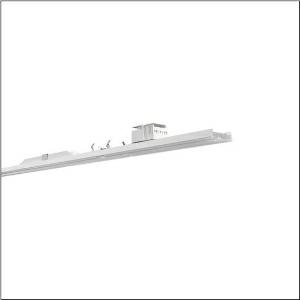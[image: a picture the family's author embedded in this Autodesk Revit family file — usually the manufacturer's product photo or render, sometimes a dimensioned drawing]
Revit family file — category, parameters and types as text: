
# Revit family: licross_r__11_recessed_mo_51tl19cn48xf_739b
name_source: partatom
category: Lighting Fixtures
units: mm (PartAtom-declared; Revit-internal decimal feet)

## family parameters
Cut with Voids When Loaded = No
Host = Face
Light Source = No
Part Type = Normal
Room Calculation Point = No
Round Connector Dimension = Use Diameter
Shared = No

## types (1)
- --- (1 x LED, 8020 lm, 48.5 W, 4000K)
    Apparent Load = 49 VA
    CIE Flux Codes = 55 90 98 100 100
    Color Rendering = 80
    Color Temperature = 4000K
    Default Elevation = 1800 mm
    Description = Licross® 11 Recessed MOluminaire insert, length: 1.500mm, width: 66mm, height: 67mm, LED rated luminous flux: 8.020lm, light colour: 840, control gear: ON/OFF Multilumen, CLOi, control gear: ECG Multilumen, with plug, 3-pole, with phase selection, mains connection: 220..240V, AC, 50/60Hz, halogen-free wiring, primary light control with lens, of plastic, primary optical cover: cover, of PMMA, light emission: direct distribution, primary light characteristic: double asymmetric, protection rating (complete): IP40, insulation class (complete): insulation class I (protective earthing), certification: CE, ENEC, VDE, protection symbol: D if used in an environment without relevant dust loads with corresponding accessories, permissible ambient temperature for indoor applications: -35..+35°C, reducing of maximum allowable ambient temperature of 5°C with ceiling mounting, corresponds to IFS (International Featured Standards) requirements for safety and quality in the food industry, packaging unit: 1 piece
    Height = 58 mm
    Lamp = 1 x LED
    Lamp Light Flux = 8020 lm
    Lamp Power = 48.5 W
    Lamp count = 1
    Length = 1500 mm
    Luminous efficacy = 165 lm/W
    Manufacturer = Siteco
    ModVariant = No
    Model = 51TL19CN48XF
    Mounting Place = Ceiling
    Mounting Type = Pendant
    Number of Poles = 1
    OnlyDefault = Yes
    Power Factor = 1
    Product Name = Licross® 11 Recessed MO
    Product group = luminaire insert
    ProductGroupID = 902
    Protection Class = Protection class I
    Protection Degree = IP 40
    RLX_Detail_Level = 1
    RlxData = <blob elided: 20125 chars, md5=416c552a>
    Socket = socket
    Standby Power = 0 W
    System Light Flux = 8020 lm
    System Power = 49 W
    Type Comments = factory setting: luminous flux: 100 % | (A | C | E) | 110 mA
    Type Image = l_1266722.jpg
    URL = http://relux.com
    VarID = @adj_138959
    Voltage = 0 V
    Weight = 0.00 kg
    Width = 66 mm

## geometry (parser evidence)
native form markers: Blend x4, Sweep x9
no freeform markers — native parametric forms only
